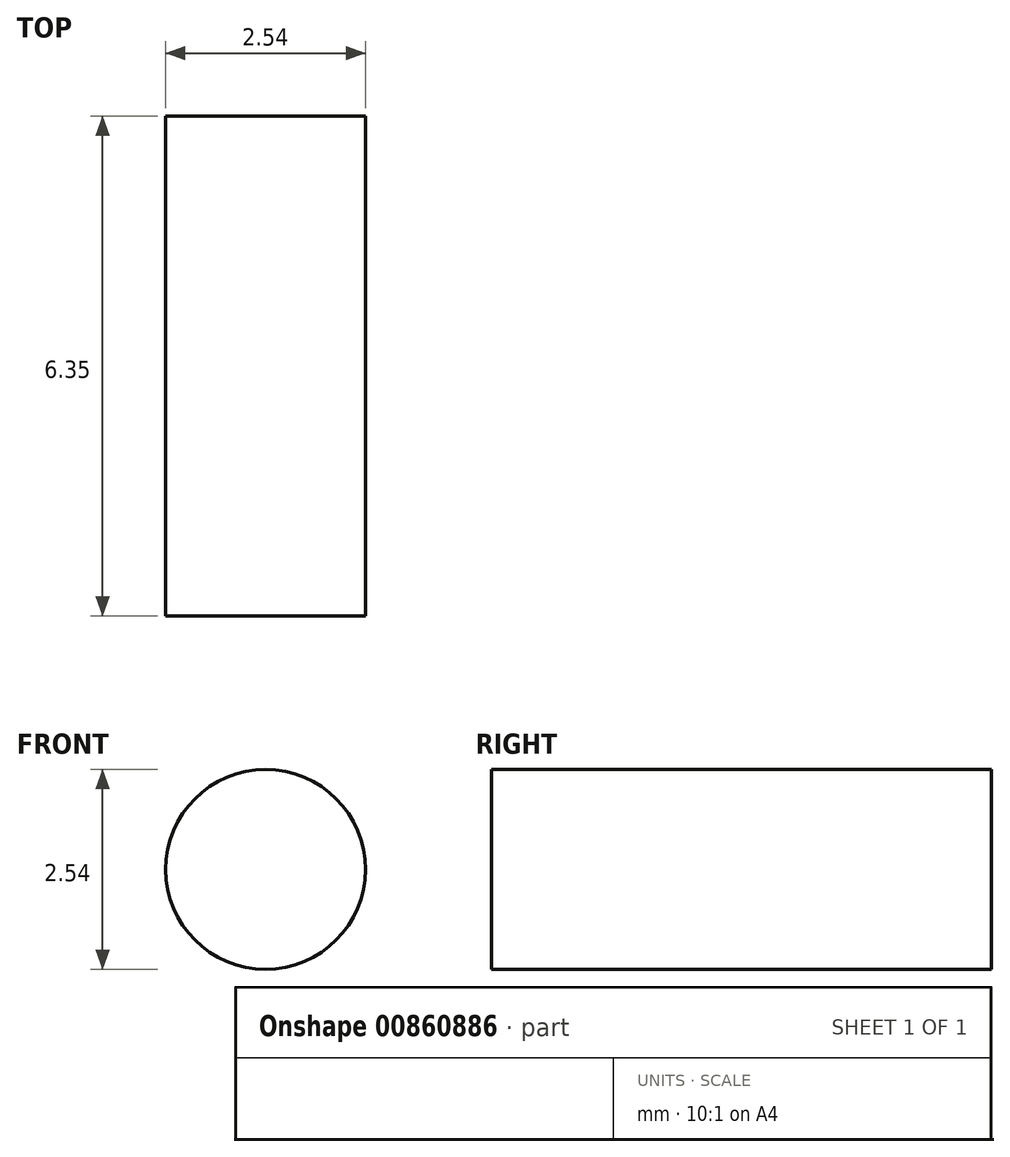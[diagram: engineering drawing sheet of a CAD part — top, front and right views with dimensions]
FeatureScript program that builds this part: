
annotation { "Feature Type Name" : "Feature", "Feature Type Description" : "" }
export const myFeature = defineFeature(function(context is Context, id is Id, definition is map)
    precondition{}
    {
        {
            var Q0;
            Q0=qCreatedBy(makeId("Front.planeOp"),FACE);
            var sketch = newSketch(context, id + "F0", { "sketchPlane" : qUnion([Q0])});
            skCircle(sketch, "E0", {"center": v(0, 0) * mm, "radius": 1.27 * mm});
            skSolve(sketch);
        }
        {
            var Q0;
            Q0 = qSketchRegion(id + "F0", true);
            extrude(context, id + "F1", {"entities" : qUnion([Q0]), "depth" : 6.35 * mm, "offsetDistance" : 25.4 * mm});
        }
    });
